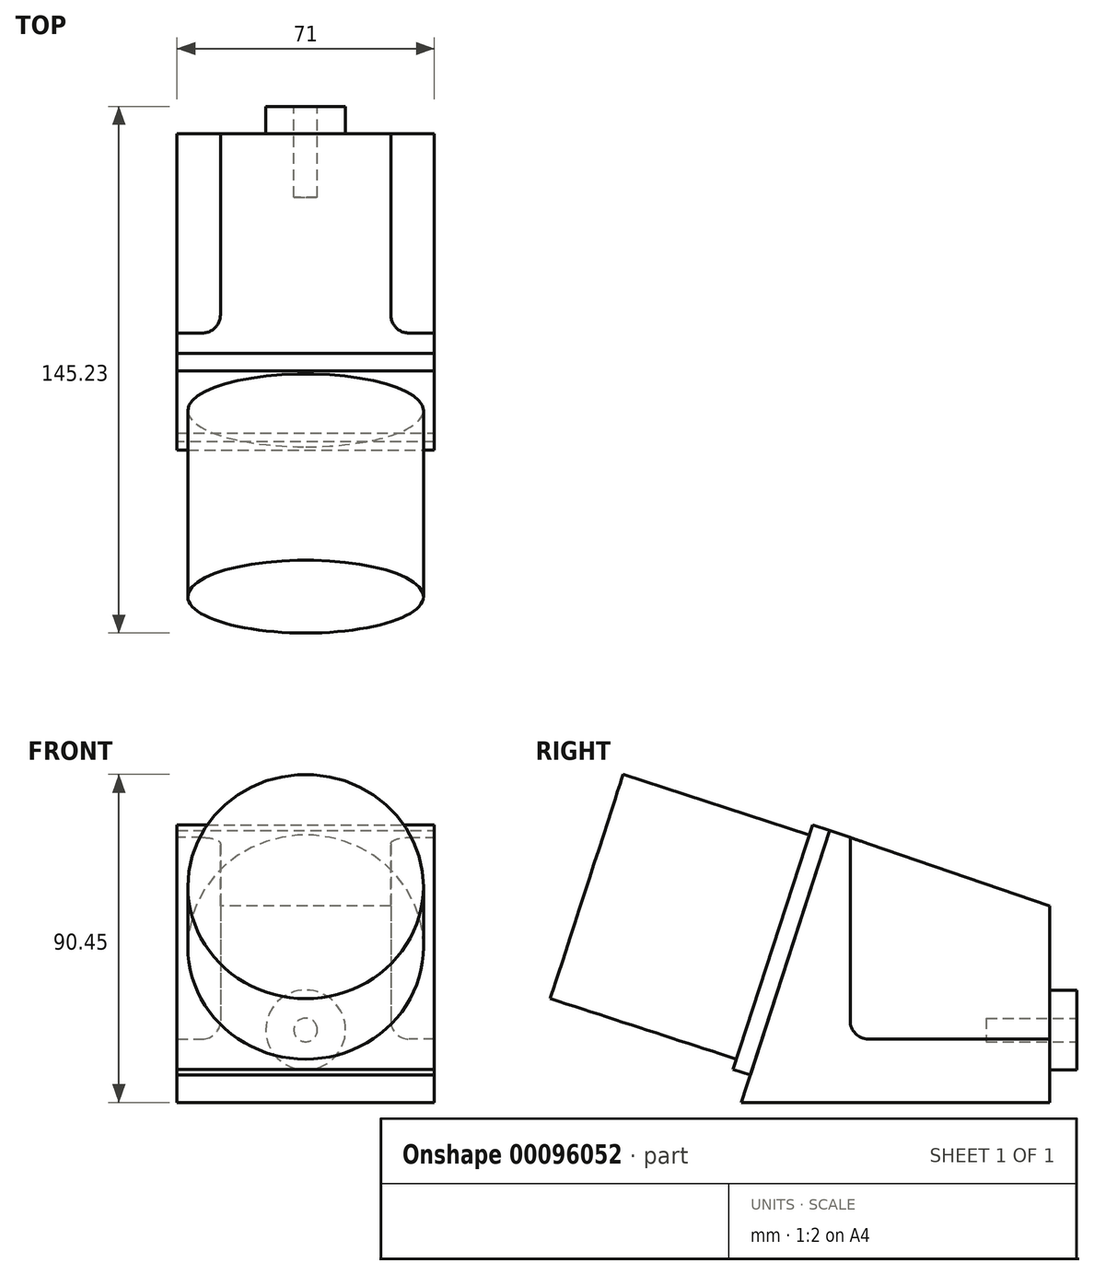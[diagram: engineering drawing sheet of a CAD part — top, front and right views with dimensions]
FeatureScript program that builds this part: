
annotation { "Feature Type Name" : "Feature", "Feature Type Description" : "" }
export const myFeature = defineFeature(function(context is Context, id is Id, definition is map)
    precondition{}
    {
        {
            var Q0;
            Q0=qCreatedBy(makeId("Top.planeOp"),FACE);
            var sketch = newSketch(context, id + "F0", { "sketchPlane" : qUnion([Q0])});
            skLineSegment(sketch, "E0.bottom", {"start": v(35.5, -42.5) * mm, "end": v(-35.5, -42.5) * mm});
            skLineSegment(sketch, "E0.top", {"start": v(35.5, 42.5) * mm, "end": v(-35.5, 42.5) * mm});
            skLineSegment(sketch, "E0.left", {"start": v(35.5, -42.5) * mm, "end": v(35.5, 42.5) * mm});
            skLineSegment(sketch, "E0.right", {"start": v(-35.5, -42.5) * mm, "end": v(-35.5, 42.5) * mm});
            skPoint(sketch, "E0.middle", {"position": v(0, 0) * mm});
            skSolve(sketch);
        }
        {
            var Q0;
            Q0 = qSketchRegion(id + "F0", true);
            extrude(context, id + "F1", {"entities" : qUnion([Q0]), "depth" : 75 * mm});
        }
        {
            var Q0;
            Q0=makeQuery(id+"F1.opExtrude","CAP_EDGE",EDGE,{"disambiguationData":[OSD([sQuery(id+"F0.wireOp",EDGE,"E0.bottom")])],"isStart":true});
            cPlane(context, id + "F2", {"entities" : qUnion([Q0]), "cplaneType" : CPlaneType.LINE_ANGLE, "offset" : 150 * mm, "angle" : 18 * degree, "width" : 150 * mm, "height" : 150 * mm});
        }
        {
            var Q0;
            Q0=qCreatedBy(id+"F2.planeOp",FACE);
            var sketch = newSketch(context, id + "F3", { "sketchPlane" : qUnion([Q0])});
            skLineSegment(sketch, "E1.bottom", {"start": v(-35.5, -13.13) * mm, "end": v(35.5, -13.13) * mm});
            skLineSegment(sketch, "E1.left", {"start": v(-35.5, -13.13) * mm, "end": v(-35.5, 90.77) * mm});
            skLineSegment(sketch, "E1.right", {"start": v(35.5, -13.13) * mm, "end": v(35.5, 90.77) * mm});
            skLineSegment(sketch, "E2", {"start": v(-35.5, 90.77) * mm, "end": v(35.5, 90.77) * mm});
            skSolve(sketch);
        }
        {
            var Q0;
            Q0 = qSketchRegion(id + "F3", true);
            extrude(context, id + "F4", {"entities" : qUnion([Q0]), "operationType" : NewBodyOperationType.REMOVE, "endBound" : BoundingType.THROUGH_ALL, "depth" : 2 * mm});
        }
        {
            var Q0;
            Q0=makeQuery(id+"F4.boolean.opBoolean","INTERSECT",EDGE,{"derivedFrom":[makeQuery(id+"F1.opExtrude","CAP_FACE",FACE,{"disambiguationData":[OSD([sQuery(id+"F0.wireOp",EDGE,"E0.bottom"),sQuery(id+"F0.wireOp",EDGE,"E0.top"),sQuery(id+"F0.wireOp",EDGE,"E0.left"),sQuery(id+"F0.wireOp",EDGE,"E0.right")])],"isStart":false}),makeQuery(id+"F4.opExtrude","CAP_FACE",FACE,{"disambiguationData":[OSD([sQuery(id+"F3.wireOp",EDGE,"E1.bottom"),sQuery(id+"F3.wireOp",EDGE,"E1.left"),sQuery(id+"F3.wireOp",EDGE,"E1.right"),sQuery(id+"F3.wireOp",EDGE,"E2")])],"isStart":true})]});
            cPlane(context, id + "F5", {"entities" : qUnion([Q0]), "cplaneType" : CPlaneType.LINE_ANGLE, "offset" : 150 * mm, "angle" : 71 * degree, "width" : 150 * mm, "height" : 150 * mm});
        }
        {
            var Q0;
            Q0=qCreatedBy(id+"F5.planeOp",FACE);
            var sketch = newSketch(context, id + "F6", { "sketchPlane" : qUnion([Q0])});
            skLineSegment(sketch, "E3.bottom", {"start": v(-35.5, -41.56) * mm, "end": v(35.5, -41.56) * mm});
            skLineSegment(sketch, "E3.top", {"start": v(-35.5, 40.18) * mm, "end": v(35.5, 40.18) * mm});
            skLineSegment(sketch, "E3.left", {"start": v(-35.5, -41.56) * mm, "end": v(-35.5, 40.18) * mm});
            skLineSegment(sketch, "E3.right", {"start": v(35.5, -41.56) * mm, "end": v(35.5, 40.18) * mm});
            skSolve(sketch);
        }
        {
            var Q0;
            Q0 = qSketchRegion(id + "F6", true);
            extrude(context, id + "F7", {"entities" : qUnion([Q0]), "operationType" : NewBodyOperationType.REMOVE, "endBound" : BoundingType.THROUGH_ALL, "depth" : 25 * mm});
        }
        {
            var Q0;
            Q0=qCreatedBy(makeId("Top.planeOp"),FACE);
            cPlane(context, id + "F8", {"entities" : qUnion([Q0]), "cplaneType" : CPlaneType.OFFSET, "offset" : 17.5 * mm, "width" : 150 * mm, "height" : 150 * mm});
        }
        {
            var Q0;
            Q0=qCreatedBy(id+"F8.planeOp",FACE);
            var sketch = newSketch(context, id + "F9", { "sketchPlane" : qUnion([Q0])});
            skLineSegment(sketch, "E4.bottom", {"start": v(-35.5, -12.5) * mm, "end": v(-23.5, -12.5) * mm});
            skLineSegment(sketch, "E4.top", {"start": v(-35.5, 42.5) * mm, "end": v(-23.5, 42.5) * mm});
            skLineSegment(sketch, "E4.left", {"start": v(-35.5, -12.5) * mm, "end": v(-35.5, 42.5) * mm});
            skLineSegment(sketch, "E4.right", {"start": v(-23.5, -12.5) * mm, "end": v(-23.5, 42.5) * mm});
            skLineSegment(sketch, "E5.MirrorCS", {"start": v(35.5, -12.5) * mm, "end": v(23.5, -12.5) * mm});
            skLineSegment(sketch, "E6.MirrorCS", {"start": v(35.5, -12.5) * mm, "end": v(35.5, 42.5) * mm});
            skLineSegment(sketch, "E7.MirrorCS", {"start": v(23.5, -12.5) * mm, "end": v(23.5, 42.5) * mm});
            skLineSegment(sketch, "E8.MirrorCS", {"start": v(35.5, 42.5) * mm, "end": v(23.5, 42.5) * mm});
            skSolve(sketch);
        }
        {
            var Q0;
            Q0 = qSketchRegion(id + "F9", true);
            extrude(context, id + "F10", {"entities" : qUnion([Q0]), "operationType" : NewBodyOperationType.REMOVE, "endBound" : BoundingType.THROUGH_ALL, "depth" : 25 * mm});
        }
        {
            var Q0;
            Q0=makeQuery(id+"F10.boolean.opBoolean","COPY",EDGE,{"derivedFrom":makeQuery(id+"F10.opExtrude","CAP_EDGE",EDGE,{"disambiguationData":[OSD([sQuery(id+"F9.wireOp",EDGE,"E4.right")])],"isStart":true})});
            var Q1;
            Q1=makeQuery(id+"F10.boolean.opBoolean","COPY",EDGE,{"derivedFrom":makeQuery(id+"F10.opExtrude","CAP_EDGE",EDGE,{"disambiguationData":[OSD([sQuery(id+"F9.wireOp",EDGE,"E4.bottom")])],"isStart":true})});
            var Q2;
            Q2=makeQuery(id+"F10.boolean.opBoolean","COPY",EDGE,{"derivedFrom":makeQuery(id+"F10.opExtrude","SWEPT_EDGE",EDGE,{"disambiguationData":[OSD([sQuery(id+"F9.wireOp",EDGE,"E4.bottom"),sQuery(id+"F9.wireOp",EDGE,"E4.right")])]})});
            var Q3;
            Q3=makeQuery(id+"F10.boolean.opBoolean","COPY",EDGE,{"derivedFrom":makeQuery(id+"F10.opExtrude","SWEPT_EDGE",EDGE,{"disambiguationData":[OSD([sQuery(id+"F9.wireOp",EDGE,"E5.MirrorCS"),sQuery(id+"F9.wireOp",EDGE,"E7.MirrorCS")])]})});
            var Q4;
            Q4=makeQuery(id+"F10.boolean.opBoolean","COPY",EDGE,{"derivedFrom":makeQuery(id+"F10.opExtrude","CAP_EDGE",EDGE,{"disambiguationData":[OSD([sQuery(id+"F9.wireOp",EDGE,"E5.MirrorCS")])],"isStart":true})});
            var Q5;
            Q5=makeQuery(id+"F10.boolean.opBoolean","COPY",EDGE,{"derivedFrom":makeQuery(id+"F10.opExtrude","CAP_EDGE",EDGE,{"disambiguationData":[OSD([sQuery(id+"F9.wireOp",EDGE,"E7.MirrorCS")])],"isStart":true})});
            fillet(context, id + "F11", {"entities" : qUnion([Q0, Q1, Q2, Q3, Q4, Q5]), "radius" : 5 * mm, "tangentPropagation" : true, "allowEdgeOverflow" : false});
        }
        {
            var Q0;
            Q0=makeQuery(id+"F1.opExtrude","SWEPT_FACE",FACE,{"disambiguationData":[OSD([sQuery(id+"F0.wireOp",EDGE,"E0.top")])]});
            var sketch = newSketch(context, id + "F12", { "sketchPlane" : qUnion([Q0])});
            skCircle(sketch, "E9", {"center": v(0, 20) * mm, "radius": 11 * mm});
            skSolve(sketch);
        }
        {
            var Q0;
            Q0 = qSketchRegion(id + "F12", true);
            extrude(context, id + "F13", {"entities" : qUnion([Q0]), "operationType" : NewBodyOperationType.ADD, "depth" : 7.5 * mm});
        }
        {
            var Q0;
            Q0=makeQuery(id+"F13.opExtrude","CAP_FACE",FACE,{"disambiguationData":[OSD([sQuery(id+"F12.wireOp",EDGE,"E9")])],"isStart":false});
            var sketch = newSketch(context, id + "F14", { "sketchPlane" : qUnion([Q0])});
            skCircle(sketch, "E10", {"center": v(0, 20) * mm, "radius": 3.25 * mm});
            skSolve(sketch);
        }
        {
            var Q0;
            Q0 = qSketchRegion(id + "F14", true);
            extrude(context, id + "F15", {"entities" : qUnion([Q0]), "operationType" : NewBodyOperationType.REMOVE, "oppositeDirection" : true, "depth" : 25 * mm});
        }
        {
            var Q0;
            Q0=makeQuery(id+"F4.boolean.opBoolean","COPY",FACE,{"derivedFrom":makeQuery(id+"F4.opExtrude","CAP_FACE",FACE,{"disambiguationData":[OSD([sQuery(id+"F3.wireOp",EDGE,"E1.bottom"),sQuery(id+"F3.wireOp",EDGE,"E1.left"),sQuery(id+"F3.wireOp",EDGE,"E1.right"),sQuery(id+"F3.wireOp",EDGE,"E2")])],"isStart":true})});
            var sketch = newSketch(context, id + "F16", { "sketchPlane" : qUnion([Q0])});
            skLineSegment(sketch, "E11.bottom", {"start": v(-35.5, 65.73) * mm, "end": v(35.5, 65.73) * mm});
            skLineSegment(sketch, "E11.top", {"start": v(-35.5, -5.13) * mm, "end": v(35.5, -5.13) * mm});
            skLineSegment(sketch, "E11.left", {"start": v(-35.5, 65.73) * mm, "end": v(-35.5, -5.13) * mm});
            skLineSegment(sketch, "E11.right", {"start": v(35.5, 65.73) * mm, "end": v(35.5, -5.13) * mm});
            skSolve(sketch);
        }
        {
            var Q0;
            Q0 = qSketchRegion(id + "F16", true);
            extrude(context, id + "F17", {"entities" : qUnion([Q0]), "depth" : 5 * mm});
        }
        {
            var Q0;
            Q0=makeQuery(id+"F17.opExtrude","CAP_FACE",FACE,{"disambiguationData":[OSD([sQuery(id+"F16.wireOp",EDGE,"E11.bottom"),sQuery(id+"F16.wireOp",EDGE,"E11.top"),sQuery(id+"F16.wireOp",EDGE,"E11.left"),sQuery(id+"F16.wireOp",EDGE,"E11.right")])],"isStart":false});
            var sketch = newSketch(context, id + "F18", { "sketchPlane" : qUnion([Q0])});
            skCircle(sketch, "E12", {"center": v(0, 30.3) * mm, "radius": 32.5 * mm});
            skLineSegment(sketch, "E13", {"start": v(-35.5, 65.73) * mm, "end": v(35.5, -5.13) * mm, "construction": true});
            skSolve(sketch);
        }
        {
            var Q0;
            Q0 = qSketchRegion(id + "F18", true);
            extrude(context, id + "F19", {"entities" : qUnion([Q0]), "operationType" : NewBodyOperationType.ADD, "depth" : 54 * mm});
        }
    });
